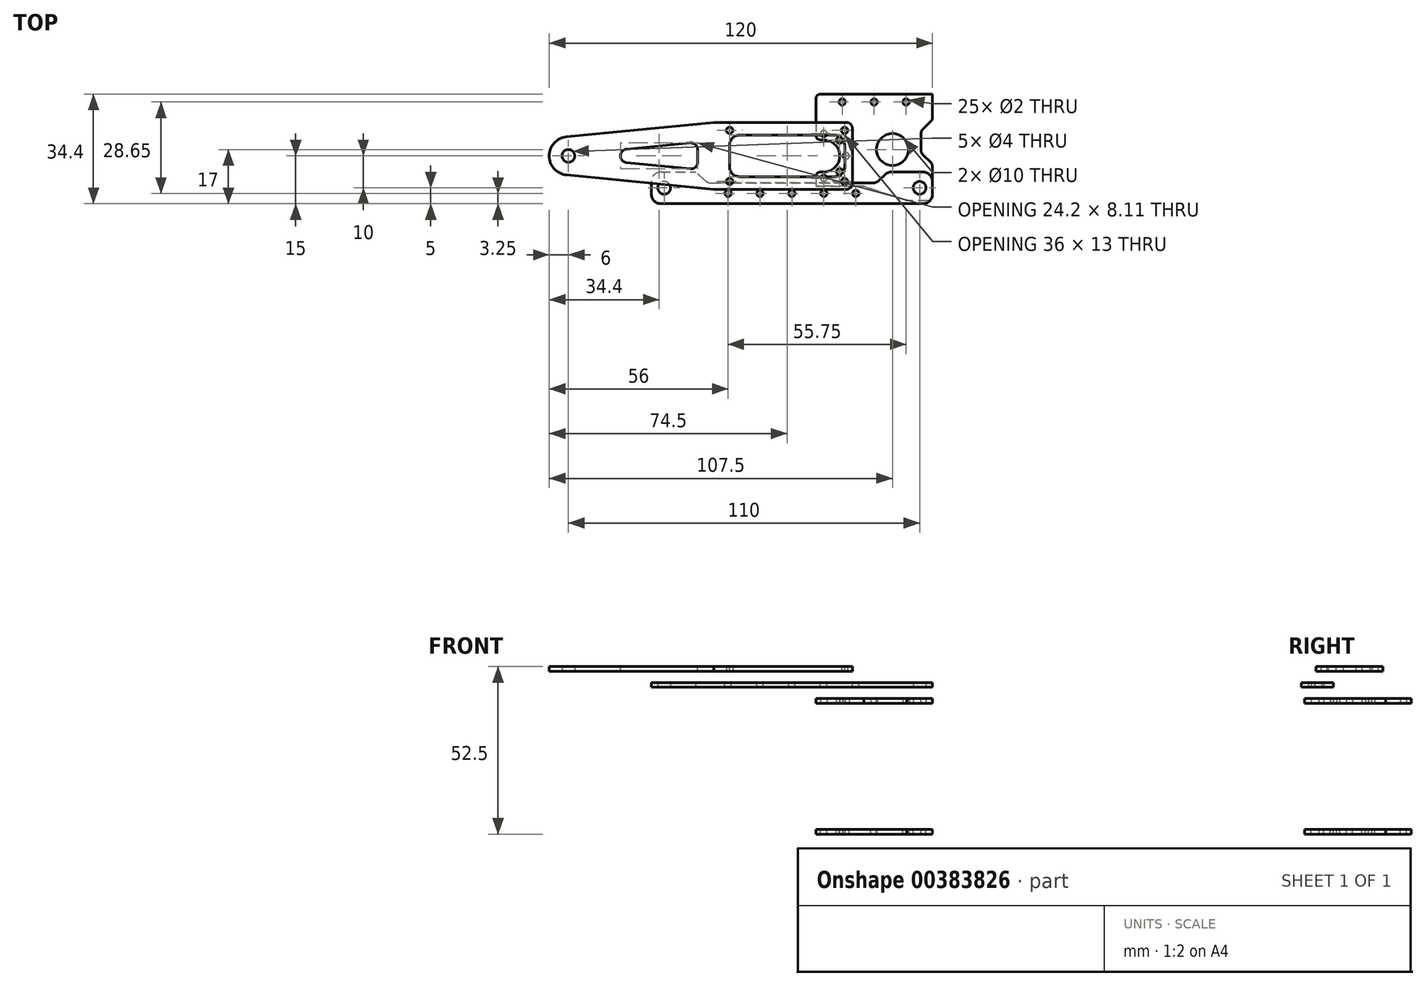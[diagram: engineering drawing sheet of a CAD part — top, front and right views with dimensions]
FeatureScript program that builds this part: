
annotation { "Feature Type Name" : "Feature", "Feature Type Description" : "" }
export const myFeature = defineFeature(function(context is Context, id is Id, definition is map)
    precondition{}
    {
        {
            var Q0;
            Q0=qCreatedBy(makeId("Top.planeOp"),FACE);
            var sketch = newSketch(context, id + "F0", { "sketchPlane" : qUnion([Q0])});
            skLineSegment(sketch, "E0.bottom", {"start": v(18.25, 16) * mm, "end": v(-18.25, 16) * mm});
            skLineSegment(sketch, "E0.top", {"start": v(18.25, -16) * mm, "end": v(-18.25, -16) * mm});
            skLineSegment(sketch, "E0.left", {"start": v(18.25, 16) * mm, "end": v(18.25, -16) * mm});
            skLineSegment(sketch, "E0.right", {"start": v(-18.25, 16) * mm, "end": v(-18.25, -16) * mm});
            skPoint(sketch, "E0.middle", {"position": v(0, 0) * mm});
            skCircle(sketch, "E1", {"center": v(14.25, -12) * mm, "radius": 2 * mm});
            skArc(sketch, "E2", {"start": v(-18.25, 2.33) * mm, "mid": v(-20.75, -2) * mm, "end": v(-18.25, -6.33) * mm, "construction": true});
            skCircle(sketch, "E3", {"center": v(-22.75, -2) * mm, "radius": 1 * mm, "construction": true});
            skCircle(sketch, "E4.1.0", {"center": v(-20.7, -6.95) * mm, "radius": 1 * mm, "construction": true});
            skCircle(sketch, "E4.2.0", {"center": v(-15.75, -9) * mm, "radius": 1 * mm});
            skCircle(sketch, "E4.3.0", {"center": v(-10.8, -6.95) * mm, "radius": 1 * mm});
            skCircle(sketch, "E4.4.0", {"center": v(-8.75, -2) * mm, "radius": 1 * mm});
            skCircle(sketch, "E4.5.0", {"center": v(-10.8, 2.95) * mm, "radius": 1 * mm});
            skCircle(sketch, "E4.6.0", {"center": v(-15.75, 5) * mm, "radius": 1 * mm});
            skCircle(sketch, "E4.7.0", {"center": v(-20.7, 2.95) * mm, "radius": 1 * mm, "construction": true});
            skLineSegment(sketch, "E5", {"start": v(-15.75, 3) * mm, "end": v(-18.25, 3) * mm});
            skLineSegment(sketch, "E6", {"start": v(-15.75, -7) * mm, "end": v(-18.25, -7) * mm});
            skArc(sketch, "E7.trimOffspring", {"start": v(-15.75, -7) * mm, "mid": v(-10.75, -2) * mm, "end": v(-15.75, 3) * mm});
            skCircle(sketch, "E8", {"center": v(-10, 14.9) * mm, "radius": 1 * mm});
            skCircle(sketch, "E9.1.0.0", {"center": v(0, 14.9) * mm, "radius": 1 * mm});
            skCircle(sketch, "E9.2.0.0", {"center": v(10, 14.9) * mm, "radius": 1 * mm});
            skLineSegment(sketch, "E9.direction1", {"start": v(-10, 14.9) * mm, "end": v(0, 14.9) * mm, "construction": true});
            skSolve(sketch);
        }
        {
            var Q0;
            {var subQ3=sQuery(id+"F0.wireOp",EDGE,"E0.bottom");Q0=makeQuery(id+"F0.imprint","IMPRINT",FACE,{"disambiguationData":[TD([[makeQuery(id+"F0.imprint","IMPRINT",EDGE,{"derivedFrom":subQ3}),1.0]])]});}
            extrude(context, id + "F1", {"entities" : qUnion([Q0]), "depth" : 1.5 * mm});
        }
        {
            var Q0;
            Q0=makeQuery(id+"F1.opExtrude","CAP_FACE",FACE,{"disambiguationData":[OSD([sQuery(id+"F0.wireOp",EDGE,"E0.bottom"),sQuery(id+"F0.wireOp",EDGE,"E0.top"),sQuery(id+"F0.wireOp",EDGE,"E0.left"),sQuery(id+"F0.wireOp",EDGE,"E0.right"),sQuery(id+"F0.wireOp",EDGE,"E1"),sQuery(id+"F0.wireOp",EDGE,"E4.2.0"),sQuery(id+"F0.wireOp",EDGE,"E4.3.0"),sQuery(id+"F0.wireOp",EDGE,"E4.4.0"),sQuery(id+"F0.wireOp",EDGE,"E4.5.0"),sQuery(id+"F0.wireOp",EDGE,"E4.6.0"),sQuery(id+"F0.wireOp",EDGE,"E5"),sQuery(id+"F0.wireOp",EDGE,"E6"),sQuery(id+"F0.wireOp",EDGE,"E7.trimOffspring")])],"isStart":true});
            var sketch = newSketch(context, id + "F2", { "sketchPlane" : qUnion([Q0])});
            skLineSegment(sketch, "E10.bottom", {"start": v(18.25, -16) * mm, "end": v(-18.25, -16) * mm});
            skLineSegment(sketch, "E10.top", {"start": v(18.25, -17.4) * mm, "end": v(-18.25, -17.4) * mm});
            skLineSegment(sketch, "E10.left", {"start": v(18.25, -16) * mm, "end": v(18.25, -17.4) * mm});
            skLineSegment(sketch, "E10.right", {"start": v(-18.25, -16) * mm, "end": v(-18.25, -17.4) * mm});
            skSolve(sketch);
        }
        {
            var Q0;
            Q0 = qSketchRegion(id + "F2", true);
            extrude(context, id + "F3", {"entities" : qUnion([Q0]), "operationType" : NewBodyOperationType.ADD, "depth" : (39.5 / 2) * mm, "hasSecondDirection" : true, "secondDirectionOppositeDirection" : true, "secondDirectionDepth" : 1.5 * mm});
        }
        {
            var Q0;
            Q0=makeQuery(id+"F3.opExtrude","CAP_FACE",FACE,{"disambiguationData":[OSD([sQuery(id+"F2.wireOp",EDGE,"E10.bottom"),sQuery(id+"F2.wireOp",EDGE,"E10.top"),sQuery(id+"F2.wireOp",EDGE,"E10.left"),sQuery(id+"F2.wireOp",EDGE,"E10.right")])],"isStart":false});
            cPlane(context, id + "F4", {"entities" : qUnion([Q0]), "cplaneType" : CPlaneType.OFFSET, "offset" : 0 * mm, "width" : 150 * mm, "height" : 150 * mm});
        }
        {
            var Q0;
            Q0=makeQuery(id+"F1.opExtrude","SWEPT_BODY",BODY,{"disambiguationData":[OSD([sQuery(id+"F0.wireOp",EDGE,"E0.bottom"),sQuery(id+"F0.wireOp",EDGE,"E0.top"),sQuery(id+"F0.wireOp",EDGE,"E0.left"),sQuery(id+"F0.wireOp",EDGE,"E0.right"),sQuery(id+"F0.wireOp",EDGE,"E1"),sQuery(id+"F0.wireOp",EDGE,"E4.2.0"),sQuery(id+"F0.wireOp",EDGE,"E4.3.0"),sQuery(id+"F0.wireOp",EDGE,"E4.4.0"),sQuery(id+"F0.wireOp",EDGE,"E4.5.0"),sQuery(id+"F0.wireOp",EDGE,"E4.6.0"),sQuery(id+"F0.wireOp",EDGE,"E5"),sQuery(id+"F0.wireOp",EDGE,"E6"),sQuery(id+"F0.wireOp",EDGE,"E7.trimOffspring")])]});
            var Q1;
            Q1=qCreatedBy(id+"F4.planeOp",FACE);
            mirror(context, id + "F5", {"operationType" : NewBodyOperationType.ADD, "entities" : qUnion([Q0]), "mirrorPlane" : qUnion([Q1])});
        }
        {
            var Q0;
            {var subQ0=makeQuery(id+"F3.opExtrude","SWEPT_FACE",FACE,{"disambiguationData":[OSD([sQuery(id+"F2.wireOp",EDGE,"E10.top")])]});Q0=makeQuery(id+"F5.boolean.opBoolean","MERGE",FACE,{"derivedFrom":[subQ0,makeQuery(id+"F5.opPattern","COPY",FACE,{"derivedFrom":subQ0,"instanceName":"1"})]});}
            var sketch = newSketch(context, id + "F6", { "sketchPlane" : qUnion([Q0])});
            skPoint(sketch, "E11.firstSnap0", {"position": v(18.25, -19.75) * mm});
            skLineSegment(sketch, "E11.bottom", {"start": v(18.25, 0) * mm, "end": v(8.25, 0) * mm});
            skLineSegment(sketch, "E11.top", {"start": v(18.25, -39.5) * mm, "end": v(8.25, -39.5) * mm});
            skLineSegment(sketch, "E11.left", {"start": v(18.25, 0) * mm, "end": v(18.25, -39.5) * mm});
            skLineSegment(sketch, "E11.right", {"start": v(8.25, 0) * mm, "end": v(8.25, -39.5) * mm});
            skSolve(sketch);
        }
        {
            var Q0;
            Q0 = qSketchRegion(id + "F6", true);
            extrude(context, id + "F7", {"entities" : qUnion([Q0]), "operationType" : NewBodyOperationType.REMOVE, "endBound" : BoundingType.UP_TO_NEXT, "oppositeDirection" : true, "depth" : 25 * mm});
        }
        {
            var Q0;
            Q0=makeQuery(id+"F3.boolean.opBoolean","MERGE",FACE,{"derivedFrom":[makeQuery(id+"F1.opExtrude","CAP_FACE",FACE,{"disambiguationData":[OSD([sQuery(id+"F0.wireOp",EDGE,"E0.bottom"),sQuery(id+"F0.wireOp",EDGE,"E0.top"),sQuery(id+"F0.wireOp",EDGE,"E0.left"),sQuery(id+"F0.wireOp",EDGE,"E0.right"),sQuery(id+"F0.wireOp",EDGE,"E1"),sQuery(id+"F0.wireOp",EDGE,"E4.2.0"),sQuery(id+"F0.wireOp",EDGE,"E4.3.0"),sQuery(id+"F0.wireOp",EDGE,"E4.4.0"),sQuery(id+"F0.wireOp",EDGE,"E4.5.0"),sQuery(id+"F0.wireOp",EDGE,"E4.6.0"),sQuery(id+"F0.wireOp",EDGE,"E5"),sQuery(id+"F0.wireOp",EDGE,"E6"),sQuery(id+"F0.wireOp",EDGE,"E7.trimOffspring")])],"isStart":false}),makeQuery(id+"F3.opExtrude","CAP_FACE",FACE,{"disambiguationData":[OSD([sQuery(id+"F2.wireOp",EDGE,"E10.bottom"),sQuery(id+"F2.wireOp",EDGE,"E10.top"),sQuery(id+"F2.wireOp",EDGE,"E10.left"),sQuery(id+"F2.wireOp",EDGE,"E10.right")])],"isStart":true})]});
            var sketch = newSketch(context, id + "F8", { "sketchPlane" : qUnion([Q0])});
            skCircle(sketch, "E12", {"center": v(-15.75, -2) * mm, "radius": 10 * mm});
            skSolve(sketch);
        }
        {
            var Q0;
            Q0=qCreatedBy(makeId("Top.planeOp"),FACE);
            cPlane(context, id + "F9", {"entities" : qUnion([Q0]), "cplaneType" : CPlaneType.OFFSET, "offset" : 5 * mm, "width" : 150 * mm, "height" : 150 * mm});
        }
        {
            var Q0;
            Q0=qCreatedBy(id+"F9.planeOp",FACE);
            var sketch = newSketch(context, id + "F10", { "sketchPlane" : qUnion([Q0])});
            skCircle(sketch, "E13.0", {"center": v(14.25, -12) * mm, "radius": 2 * mm});
            skLineSegment(sketch, "E14.bottom", {"start": v(-69.75, -7) * mm, "end": v(18.25, -7) * mm});
            skLineSegment(sketch, "E14.top", {"start": v(-69.75, -17) * mm, "end": v(18.25, -17) * mm});
            skLineSegment(sketch, "E14.left", {"start": v(-69.75, -7) * mm, "end": v(-69.75, -17) * mm});
            skLineSegment(sketch, "E14.right", {"start": v(18.25, -7) * mm, "end": v(18.25, -17) * mm});
            skLineSegment(sketch, "E15", {"start": v(-25.75, -7) * mm, "end": v(-25.75, -17) * mm, "construction": true});
            skCircle(sketch, "E16.MirrorC", {"center": v(-65.75, -12) * mm, "radius": 2 * mm});
            skLineSegment(sketch, "E17.bottom", {"start": v(-40.75, -7) * mm, "end": v(-10.75, -7) * mm});
            skLineSegment(sketch, "E17.top", {"start": v(-40.75, -9) * mm, "end": v(-10.75, -9) * mm});
            skLineSegment(sketch, "E17.left", {"start": v(-40.75, -7) * mm, "end": v(-40.75, -9) * mm});
            skLineSegment(sketch, "E17.right", {"start": v(-10.75, -7) * mm, "end": v(-10.75, -9) * mm});
            skPoint(sketch, "E17.middle", {"position": v(-25.75, -8) * mm});
            skSolve(sketch);
        }
        {
            var Q0;
            Q0=makeQuery(id+"F10.imprint","IMPRINT",FACE,{"disambiguationData":[TD([[makeQuery(id+"F10.imprint","IMPRINT",EDGE,{"derivedFrom":sQuery(id+"F10.wireOp",EDGE,"E13.0")}),-1.0]])]});
            var Q1;
            Q1=makeQuery(id+"F10.imprint","IMPRINT",FACE,{"disambiguationData":[TD([[makeQuery(id+"F10.imprint","IMPRINT",EDGE,{"derivedFrom":sQuery(id+"F10.wireOp",EDGE,"E17.top")}),1.0]])]});
            extrude(context, id + "F11", {"entities" : qUnion([Q0, Q1]), "depth" : 1.5 * mm});
        }
        {
            var Q0;
            Q0=qCreatedBy(makeId("Top.planeOp"),FACE);
            cPlane(context, id + "F12", {"entities" : qUnion([Q0]), "cplaneType" : CPlaneType.OFFSET, "offset" : 10 * mm, "width" : 150 * mm, "height" : 150 * mm});
        }
        {
            var Q0;
            Q0=qCreatedBy(id+"F12.planeOp",FACE);
            var sketch = newSketch(context, id + "F13", { "sketchPlane" : qUnion([Q0])});
            skCircle(sketch, "E18.0", {"center": v(-15.75, -2) * mm, "radius": 10 * mm, "construction": true});
            skLineSegment(sketch, "E19.bottom", {"start": v(-45.25, 6) * mm, "end": v(-9.25, 6) * mm, "construction": true});
            skLineSegment(sketch, "E19.top", {"start": v(-45.25, -10) * mm, "end": v(-9.25, -10) * mm, "construction": true});
            skLineSegment(sketch, "E19.left", {"start": v(-45.25, 6) * mm, "end": v(-45.25, -10) * mm, "construction": true});
            skLineSegment(sketch, "E19.right", {"start": v(-9.25, 6) * mm, "end": v(-9.25, -10) * mm, "construction": true});
            skPoint(sketch, "E19.middle", {"position": v(-27.25, -2) * mm});
            skCircle(sketch, "E20", {"center": v(-9.25, 6) * mm, "radius": 1 * mm});
            skCircle(sketch, "E21", {"center": v(-9.25, -10) * mm, "radius": 1 * mm});
            skCircle(sketch, "E22", {"center": v(-45.25, -10) * mm, "radius": 1 * mm});
            skCircle(sketch, "E23", {"center": v(-45.25, 6) * mm, "radius": 1 * mm});
            skLineSegment(sketch, "E24.bottom", {"start": v(-6.75, -12.5) * mm, "end": v(-101.75, -12.5) * mm});
            skLineSegment(sketch, "E24.top", {"start": v(-6.75, 8.5) * mm, "end": v(-101.75, 8.5) * mm});
            skLineSegment(sketch, "E24.left", {"start": v(-6.75, -12.5) * mm, "end": v(-6.75, 8.5) * mm});
            skLineSegment(sketch, "E24.right", {"start": v(-101.75, -12.5) * mm, "end": v(-101.75, 8.5) * mm});
            skPoint(sketch, "E25", {"position": v(-6.75, -2) * mm});
            skCircle(sketch, "E26", {"center": v(-95.75, -2) * mm, "radius": 2 * mm});
            skLineSegment(sketch, "E27", {"start": v(-95.75, -2) * mm, "end": v(-15.75, -2) * mm, "construction": true});
            skCircle(sketch, "E28.0", {"center": v(-65.75, -12) * mm, "radius": 2 * mm, "construction": true});
            skCircle(sketch, "E29.0", {"center": v(14.25, -12) * mm, "radius": 2 * mm, "construction": true});
            skLineSegment(sketch, "E30", {"start": v(-65.75, -12) * mm, "end": v(14.25, -12) * mm, "construction": true});
            skSolve(sketch);
        }
        {
            var Q0;
            Q0 = qSketchRegion(id + "F13", true);
            extrude(context, id + "F14", {"entities" : qUnion([Q0]), "operationType" : NewBodyOperationType.ADD, "depth" : 1.5 * mm});
        }
        {
            var Q0;
            Q0=makeQuery(id+"F14.opExtrude","CAP_FACE",FACE,{"disambiguationData":[OSD([sQuery(id+"F13.wireOp",EDGE,"E20"),sQuery(id+"F13.wireOp",EDGE,"E21"),sQuery(id+"F13.wireOp",EDGE,"E22"),sQuery(id+"F13.wireOp",EDGE,"E23"),sQuery(id+"F13.wireOp",EDGE,"E24.bottom"),sQuery(id+"F13.wireOp",EDGE,"E24.top"),sQuery(id+"F13.wireOp",EDGE,"E24.left"),sQuery(id+"F13.wireOp",EDGE,"E24.right"),sQuery(id+"F13.wireOp",EDGE,"E26")])],"isStart":false});
            var sketch = newSketch(context, id + "F15", { "sketchPlane" : qUnion([Q0])});
            skCircle(sketch, "E31", {"center": v(-95.75, -2) * mm, "radius": 6 * mm});
            skLineSegment(sketch, "E32", {"start": v(-50.25, 8.5) * mm, "end": v(-96.34, 3.97) * mm});
            skLineSegment(sketch, "E33", {"start": v(-6.75, -2) * mm, "end": v(-101.75, -2) * mm, "construction": true});
            skLineSegment(sketch, "E34.MirrorCS", {"start": v(-50.25, -12.5) * mm, "end": v(-96.34, -7.97) * mm});
            skLineSegment(sketch, "E35", {"start": v(-50.25, 8.5) * mm, "end": v(-101.75, 8.5) * mm});
            skLineSegment(sketch, "E36", {"start": v(-101.75, 8.5) * mm, "end": v(-101.75, -12.5) * mm});
            skLineSegment(sketch, "E37", {"start": v(-101.75, -12.5) * mm, "end": v(-50.25, -12.5) * mm});
            skCircle(sketch, "E38.0", {"center": v(-45.25, -10) * mm, "radius": 1 * mm, "construction": true});
            skLineSegment(sketch, "E39", {"start": v(-77.56, 0.09) * mm, "end": v(-57.56, 2.06) * mm});
            skLineSegment(sketch, "E40", {"start": v(-55.25, -0.03) * mm, "end": v(-55.25, -2) * mm});
            skLineSegment(sketch, "E41.MirrorCS", {"start": v(-55.25, -3.97) * mm, "end": v(-55.25, -2) * mm});
            skLineSegment(sketch, "E42.MirrorCS", {"start": v(-77.56, -4.09) * mm, "end": v(-57.56, -6.06) * mm});
            skPoint(sketch, "E43.visualSharp", {"position": v(-55.25, 2.28) * mm});
            skArc(sketch, "E43.filletArc", {"start": v(-55.25, -0.03) * mm, "mid": v(-55.94, 1.52) * mm, "end": v(-57.56, 2.06) * mm});
            skPoint(sketch, "E44.visualSharp", {"position": v(-55.25, -6.28) * mm});
            skArc(sketch, "E44.filletArc", {"start": v(-57.56, -6.06) * mm, "mid": v(-55.94, -5.52) * mm, "end": v(-55.25, -3.97) * mm});
            skPoint(sketch, "E45.visualSharp", {"position": v(-98.82, -2) * mm});
            skArc(sketch, "E45.filletArc", {"start": v(-77.56, 0.09) * mm, "mid": v(-79.45, -2) * mm, "end": v(-77.56, -4.09) * mm});
            skSolve(sketch);
        }
        {
            var Q0;
            {var subQ0=sQuery(id+"F15.wireOp",EDGE,"E32");Q0=makeQuery(id+"F15.imprint","IMPRINT",FACE,{"disambiguationData":[TD([[makeQuery(id+"F15.imprint","IMPRINT",EDGE,{"derivedFrom":subQ0}),-1.0]])]});}
            var Q1;
            {var subQ0=sQuery(id+"F15.wireOp",EDGE,"E34.MirrorCS");Q1=makeQuery(id+"F15.imprint","IMPRINT",FACE,{"disambiguationData":[TD([[makeQuery(id+"F15.imprint","IMPRINT",EDGE,{"derivedFrom":subQ0}),1.0]])]});}
            var Q2;
            Q2=makeQuery(id+"F15.imprint","IMPRINT",FACE,{"disambiguationData":[TD([[makeQuery(id+"F15.imprint","IMPRINT",EDGE,{"derivedFrom":sQuery(id+"F15.wireOp",EDGE,"E39")}),-1.0]])]});
            extrude(context, id + "F16", {"entities" : qUnion([Q0, Q1, Q2]), "operationType" : NewBodyOperationType.REMOVE, "endBound" : BoundingType.UP_TO_NEXT, "oppositeDirection" : true, "depth" : 25 * mm});
        }
        {
            var Q0;
            Q0=qCreatedBy(makeId("Top.planeOp"),FACE);
            cPlane(context, id + "F17", {"entities" : qUnion([Q0]), "cplaneType" : CPlaneType.OFFSET, "offset" : 50 * mm, "oppositeDirection" : true, "width" : 150 * mm, "height" : 150 * mm});
        }
        {
            var Q0;
            Q0=makeQuery(id+"F1.opExtrude","SWEPT_BODY",BODY,{"disambiguationData":[OSD([sQuery(id+"F0.wireOp",EDGE,"E0.bottom"),sQuery(id+"F0.wireOp",EDGE,"E0.top"),sQuery(id+"F0.wireOp",EDGE,"E0.left"),sQuery(id+"F0.wireOp",EDGE,"E0.right"),sQuery(id+"F0.wireOp",EDGE,"E1"),sQuery(id+"F0.wireOp",EDGE,"E4.2.0"),sQuery(id+"F0.wireOp",EDGE,"E4.3.0"),sQuery(id+"F0.wireOp",EDGE,"E4.4.0"),sQuery(id+"F0.wireOp",EDGE,"E4.5.0"),sQuery(id+"F0.wireOp",EDGE,"E4.6.0"),sQuery(id+"F0.wireOp",EDGE,"E5"),sQuery(id+"F0.wireOp",EDGE,"E6"),sQuery(id+"F0.wireOp",EDGE,"E7.trimOffspring")])]});
            var Q1;
            Q1=qCreatedBy(id+"F17.planeOp",FACE);
            mirror(context, id + "F18", {"entities" : qUnion([Q0]), "mirrorPlane" : qUnion([Q1])});
        }
        {
            var Q0;
            Q0=makeQuery(id+"F3.boolean.opBoolean","MERGE",FACE,{"derivedFrom":[makeQuery(id+"F1.opExtrude","CAP_FACE",FACE,{"disambiguationData":[OSD([sQuery(id+"F0.wireOp",EDGE,"E0.bottom"),sQuery(id+"F0.wireOp",EDGE,"E0.top"),sQuery(id+"F0.wireOp",EDGE,"E0.left"),sQuery(id+"F0.wireOp",EDGE,"E0.right"),sQuery(id+"F0.wireOp",EDGE,"E1"),sQuery(id+"F0.wireOp",EDGE,"E4.2.0"),sQuery(id+"F0.wireOp",EDGE,"E4.3.0"),sQuery(id+"F0.wireOp",EDGE,"E4.4.0"),sQuery(id+"F0.wireOp",EDGE,"E4.5.0"),sQuery(id+"F0.wireOp",EDGE,"E4.6.0"),sQuery(id+"F0.wireOp",EDGE,"E5"),sQuery(id+"F0.wireOp",EDGE,"E6"),sQuery(id+"F0.wireOp",EDGE,"E7.trimOffspring")])],"isStart":false}),makeQuery(id+"F3.opExtrude","CAP_FACE",FACE,{"disambiguationData":[OSD([sQuery(id+"F2.wireOp",EDGE,"E10.bottom"),sQuery(id+"F2.wireOp",EDGE,"E10.top"),sQuery(id+"F2.wireOp",EDGE,"E10.left"),sQuery(id+"F2.wireOp",EDGE,"E10.right")])],"isStart":true})]});
            var sketch = newSketch(context, id + "F19", { "sketchPlane" : qUnion([Q0])});
            skCircle(sketch, "E46.0", {"center": v(-15.75, -9) * mm, "radius": 1 * mm, "construction": true});
            skLineSegment(sketch, "E47", {"start": v(-18.25, -11.5) * mm, "end": v(-3.25, -11.5) * mm});
            skLineSegment(sketch, "E48", {"start": v(-3.25, -11.5) * mm, "end": v(10.25, -16) * mm});
            skCircle(sketch, "E49.0", {"center": v(14.25, -12) * mm, "radius": 2 * mm, "construction": true});
            skLineSegment(sketch, "E50", {"start": v(18.25, 9.4) * mm, "end": v(14.75, 5.9) * mm});
            skLineSegment(sketch, "E51", {"start": v(14.75, 5.9) * mm, "end": v(14.75, 2.4) * mm});
            skLineSegment(sketch, "E52", {"start": v(14.75, 2.4) * mm, "end": v(18.25, 2.4) * mm, "construction": true});
            skLineSegment(sketch, "E53.MirrorCS", {"start": v(14.75, -1.1) * mm, "end": v(14.75, 2.4) * mm});
            skLineSegment(sketch, "E54.MirrorCS", {"start": v(18.25, -4.6) * mm, "end": v(14.75, -1.1) * mm});
            skLineSegment(sketch, "E55", {"start": v(18.25, 9.4) * mm, "end": v(18.25, -4.6) * mm});
            skCircle(sketch, "E56", {"center": v(5.75, 0) * mm, "radius": 5 * mm});
            skSolve(sketch);
        }
        {
            var Q0;
            Q0 = qSketchRegion(id + "F19", true);
            var Q1;
            {var subQ0=sQuery(id+"F19.wireOp",EDGE,"E47");Q1=makeQuery(id+"F19.imprint","IMPRINT",FACE,{"disambiguationData":[TD([[makeQuery(id+"F19.imprint","IMPRINT",EDGE,{"derivedFrom":subQ0}),-1.0]])]});}
            var Q2;
            Q2=makeQuery(id+"F18.opPattern","COPY",FACE,{"derivedFrom":makeQuery(id+"F3.boolean.opBoolean","MERGE",FACE,{"derivedFrom":[makeQuery(id+"F1.opExtrude","CAP_FACE",FACE,{"disambiguationData":[OSD([sQuery(id+"F0.wireOp",EDGE,"E0.bottom"),sQuery(id+"F0.wireOp",EDGE,"E0.top"),sQuery(id+"F0.wireOp",EDGE,"E0.left"),sQuery(id+"F0.wireOp",EDGE,"E0.right"),sQuery(id+"F0.wireOp",EDGE,"E1"),sQuery(id+"F0.wireOp",EDGE,"E4.2.0"),sQuery(id+"F0.wireOp",EDGE,"E4.3.0"),sQuery(id+"F0.wireOp",EDGE,"E4.4.0"),sQuery(id+"F0.wireOp",EDGE,"E4.5.0"),sQuery(id+"F0.wireOp",EDGE,"E4.6.0"),sQuery(id+"F0.wireOp",EDGE,"E5"),sQuery(id+"F0.wireOp",EDGE,"E6"),sQuery(id+"F0.wireOp",EDGE,"E7.trimOffspring")])],"isStart":false}),makeQuery(id+"F3.opExtrude","CAP_FACE",FACE,{"disambiguationData":[OSD([sQuery(id+"F2.wireOp",EDGE,"E10.bottom"),sQuery(id+"F2.wireOp",EDGE,"E10.top"),sQuery(id+"F2.wireOp",EDGE,"E10.left"),sQuery(id+"F2.wireOp",EDGE,"E10.right")])],"isStart":true})]}),"instanceName":"1"});
            extrude(context, id + "F20", {"entities" : qUnion([Q0, Q1]), "operationType" : NewBodyOperationType.REMOVE, "endBound" : BoundingType.THROUGH_ALL, "oppositeDirection" : true, "endBoundEntityFace" : qUnion([Q2]), "depth" : 25 * mm});
        }
        {
            var Q0;
            Q0=makeQuery(id+"F11.opExtrude","CAP_FACE",FACE,{"disambiguationData":[OSD([sQuery(id+"F10.wireOp",EDGE,"E13.0"),sQuery(id+"F10.wireOp",EDGE,"E14.bottom"),sQuery(id+"F10.wireOp",EDGE,"E14.top"),sQuery(id+"F10.wireOp",EDGE,"E14.left"),sQuery(id+"F10.wireOp",EDGE,"E14.right"),sQuery(id+"F10.wireOp",EDGE,"E16.MirrorC")])],"isStart":false});
            var sketch = newSketch(context, id + "F21", { "sketchPlane" : qUnion([Q0])});
            skLineSegment(sketch, "E57", {"start": v(-55.75, -7) * mm, "end": v(-52.25, -10.5) * mm});
            skLineSegment(sketch, "E58", {"start": v(-52.25, -10.5) * mm, "end": v(-25.75, -10.5) * mm});
            skLineSegment(sketch, "E59", {"start": v(-25.75, -7) * mm, "end": v(-25.75, -17) * mm, "construction": true});
            skLineSegment(sketch, "E60", {"start": v(-69.75, -12) * mm, "end": v(18.25, -12) * mm, "construction": true});
            skCircle(sketch, "E61.0", {"center": v(-65.75, -12) * mm, "radius": 2 * mm, "construction": true});
            skLineSegment(sketch, "E62.MirrorCS", {"start": v(0.75, -10.5) * mm, "end": v(-25.75, -10.5) * mm});
            skLineSegment(sketch, "E63.MirrorCS", {"start": v(4.25, -7) * mm, "end": v(0.75, -10.5) * mm});
            skLineSegment(sketch, "E64", {"start": v(-55.75, -7) * mm, "end": v(4.25, -7) * mm});
            skSolve(sketch);
        }
        {
            var Q0;
            Q0 = qSketchRegion(id + "F21", true);
            extrude(context, id + "F22", {"entities" : qUnion([Q0]), "operationType" : NewBodyOperationType.REMOVE, "endBound" : BoundingType.UP_TO_NEXT, "oppositeDirection" : true, "depth" : 25 * mm});
        }
        {
            var Q0;
            Q0=makeQuery(id+"F11.opExtrude","SWEPT_EDGE",EDGE,{"disambiguationData":[OSD([sQuery(id+"F10.wireOp",EDGE,"E14.bottom"),sQuery(id+"F10.wireOp",EDGE,"E14.left")])]});
            var Q1;
            Q1=makeQuery(id+"F11.opExtrude","SWEPT_EDGE",EDGE,{"disambiguationData":[OSD([sQuery(id+"F10.wireOp",EDGE,"E14.top"),sQuery(id+"F10.wireOp",EDGE,"E14.left")])]});
            var Q2;
            Q2=makeQuery(id+"F11.opExtrude","SWEPT_EDGE",EDGE,{"disambiguationData":[OSD([sQuery(id+"F10.wireOp",EDGE,"E14.bottom"),sQuery(id+"F10.wireOp",EDGE,"E14.right")])]});
            var Q3;
            Q3=makeQuery(id+"F11.opExtrude","SWEPT_EDGE",EDGE,{"disambiguationData":[OSD([sQuery(id+"F10.wireOp",EDGE,"E14.top"),sQuery(id+"F10.wireOp",EDGE,"E14.right")])]});
            var Q4;
            Q4=makeQuery(id+"F22.boolean.opBoolean","COPY",EDGE,{"derivedFrom":makeQuery(id+"F22.opExtrude","SWEPT_EDGE",EDGE,{"disambiguationData":[OSD([sQuery(id+"F10.wireOp",EDGE,"E14.bottom"),sQuery(id+"F21.wireOp",EDGE,"E57"),sQuery(id+"F21.wireOp",EDGE,"E64")])]})});
            var Q5;
            Q5=makeQuery(id+"F22.boolean.opBoolean","COPY",EDGE,{"derivedFrom":makeQuery(id+"F22.opExtrude","SWEPT_EDGE",EDGE,{"disambiguationData":[OSD([sQuery(id+"F21.wireOp",EDGE,"E57"),sQuery(id+"F21.wireOp",EDGE,"E58")])]})});
            var Q6;
            Q6=makeQuery(id+"F22.boolean.opBoolean","COPY",EDGE,{"derivedFrom":makeQuery(id+"F22.opExtrude","SWEPT_EDGE",EDGE,{"disambiguationData":[OSD([sQuery(id+"F21.wireOp",EDGE,"E62.MirrorCS"),sQuery(id+"F21.wireOp",EDGE,"E63.MirrorCS")])]})});
            var Q7;
            Q7=makeQuery(id+"F22.boolean.opBoolean","COPY",EDGE,{"derivedFrom":makeQuery(id+"F22.opExtrude","SWEPT_EDGE",EDGE,{"disambiguationData":[OSD([sQuery(id+"F10.wireOp",EDGE,"E14.bottom"),sQuery(id+"F21.wireOp",EDGE,"E63.MirrorCS"),sQuery(id+"F21.wireOp",EDGE,"E64")])]})});
            fillet(context, id + "F23", {"entities" : qUnion([Q0, Q1, Q2, Q3, Q4, Q5, Q6, Q7]), "radius" : 3 * mm, "tangentPropagation" : true, "allowEdgeOverflow" : false});
        }
        {
            var Q0;
            Q0=makeQuery(id+"F14.opExtrude","CAP_FACE",FACE,{"disambiguationData":[OSD([sQuery(id+"F13.wireOp",EDGE,"E20"),sQuery(id+"F13.wireOp",EDGE,"E21"),sQuery(id+"F13.wireOp",EDGE,"E22"),sQuery(id+"F13.wireOp",EDGE,"E23"),sQuery(id+"F13.wireOp",EDGE,"E24.bottom"),sQuery(id+"F13.wireOp",EDGE,"E24.top"),sQuery(id+"F13.wireOp",EDGE,"E24.left"),sQuery(id+"F13.wireOp",EDGE,"E24.right"),sQuery(id+"F13.wireOp",EDGE,"E26")])],"isStart":false});
            var sketch = newSketch(context, id + "F24", { "sketchPlane" : qUnion([Q0])});
            skLineSegment(sketch, "E65.bottom", {"start": v(-42.25, 4.5) * mm, "end": v(-12.25, 4.5) * mm});
            skLineSegment(sketch, "E65.top", {"start": v(-42.25, -8.5) * mm, "end": v(-12.25, -8.5) * mm});
            skLineSegment(sketch, "E65.left", {"start": v(-45.25, 1.5) * mm, "end": v(-45.25, -5.5) * mm});
            skLineSegment(sketch, "E65.right", {"start": v(-9.25, 1.5) * mm, "end": v(-9.25, -5.5) * mm});
            skPoint(sketch, "E65.middle", {"position": v(-27.25, -2) * mm});
            skPoint(sketch, "E65.middle.positionSnap0", {"position": v(-6.75, -2) * mm});
            skPoint(sketch, "E65.centerSnap0", {"position": v(-6.75, -2) * mm});
            skLineSegment(sketch, "E66", {"start": v(-45.25, 6) * mm, "end": v(-9.25, 6) * mm, "construction": true});
            skPoint(sketch, "E67", {"position": v(-27.25, 6) * mm});
            skPoint(sketch, "E68.visualSharp", {"position": v(-45.25, 4.5) * mm});
            skArc(sketch, "E68.filletArc", {"start": v(-42.25, 4.5) * mm, "mid": v(-44.37, 3.62) * mm, "end": v(-45.25, 1.5) * mm});
            skPoint(sketch, "E69.visualSharp", {"position": v(-45.25, -8.5) * mm});
            skArc(sketch, "E69.filletArc", {"start": v(-45.25, -5.5) * mm, "mid": v(-44.37, -7.62) * mm, "end": v(-42.25, -8.5) * mm});
            skPoint(sketch, "E70.visualSharp", {"position": v(-9.25, 4.5) * mm});
            skArc(sketch, "E70.filletArc", {"start": v(-9.25, 1.5) * mm, "mid": v(-10.13, 3.62) * mm, "end": v(-12.25, 4.5) * mm});
            skPoint(sketch, "E71.visualSharp", {"position": v(-9.25, -8.5) * mm});
            skArc(sketch, "E71.filletArc", {"start": v(-12.25, -8.5) * mm, "mid": v(-10.13, -7.62) * mm, "end": v(-9.25, -5.5) * mm});
            skLineSegment(sketch, "E72", {"start": v(-95.75, -2) * mm, "end": v(-45.25, -2) * mm, "construction": true});
            skSolve(sketch);
        }
        {
            var Q0;
            Q0=makeQuery(id+"F24.imprint","IMPRINT",FACE,{"disambiguationData":[TD([[makeQuery(id+"F24.imprint","IMPRINT",EDGE,{"derivedFrom":sQuery(id+"F24.wireOp",EDGE,"E65.bottom")}),-1.0]])]});
            extrude(context, id + "F25", {"entities" : qUnion([Q0]), "operationType" : NewBodyOperationType.REMOVE, "endBound" : BoundingType.UP_TO_NEXT, "oppositeDirection" : true, "depth" : 25 * mm, "offsetDistance" : 25 * mm});
        }
        {
            var Q0;
            Q0=makeQuery(id+"F16.boolean.opBoolean","COPY",EDGE,{"derivedFrom":makeQuery(id+"F16.opExtrude","SWEPT_EDGE",EDGE,{"disambiguationData":[OSD([sQuery(id+"F13.wireOp",EDGE,"E24.top"),sQuery(id+"F15.wireOp",EDGE,"E32"),sQuery(id+"F15.wireOp",EDGE,"E35")])]})});
            var Q1;
            Q1=makeQuery(id+"F16.boolean.opBoolean","COPY",EDGE,{"derivedFrom":makeQuery(id+"F16.opExtrude","SWEPT_EDGE",EDGE,{"disambiguationData":[OSD([sQuery(id+"F13.wireOp",EDGE,"E24.bottom"),sQuery(id+"F15.wireOp",EDGE,"E34.MirrorCS"),sQuery(id+"F15.wireOp",EDGE,"E37")])]})});
            var Q2;
            Q2=makeQuery(id+"F14.opExtrude","SWEPT_EDGE",EDGE,{"disambiguationData":[OSD([sQuery(id+"F13.wireOp",EDGE,"E24.bottom"),sQuery(id+"F13.wireOp",EDGE,"E24.left")])]});
            var Q3;
            Q3=makeQuery(id+"F14.opExtrude","SWEPT_EDGE",EDGE,{"disambiguationData":[OSD([sQuery(id+"F13.wireOp",EDGE,"E24.top"),sQuery(id+"F13.wireOp",EDGE,"E24.left")])]});
            fillet(context, id + "F26", {"entities" : qUnion([Q0, Q1, Q2, Q3]), "radius" : 2 * mm, "tangentPropagation" : true, "allowEdgeOverflow" : false});
        }
        {
            var Q0;
            {var subQ0=sQuery(id+"F0.wireOp",EDGE,"E0.right");var subQ1=sQuery(id+"F19.wireOp",EDGE,"E47");Q0=makeQuery(id+"F20.boolean.opBoolean","COPY",EDGE,{"disambiguationData":[topologyDisambiguationEdgeConnected([makeQuery(id+"F5.opPattern","COPY",FACE,{"derivedFrom":makeQuery(id+"F1.opExtrude","SWEPT_FACE",FACE,{"disambiguationData":[OSD([subQ0]),TDD([makeQuery(id+"F0.imprint","IMPRINT",EDGE,{"disambiguationData":[TD([[makeQuery(id+"F0.imprint","INTERSECT",VERTEX,{"derivedFrom":[sQuery(id+"F0.wireOp",EDGE,"E0.top"),subQ0]}),1.0]])],"derivedFrom":subQ0})])]}),"instanceName":"1"})])],"derivedFrom":makeQuery(id+"F20.opExtrude","SWEPT_EDGE",EDGE,{"disambiguationData":[OSD([subQ0,subQ1])]})});}
            var Q1;
            {var subQ0=sQuery(id+"F0.wireOp",EDGE,"E9.2.0.0");var subQ1=sQuery(id+"F0.wireOp",EDGE,"E9.1.0.0");var subQ2=sQuery(id+"F0.wireOp",EDGE,"E8");var subQ3=sQuery(id+"F0.wireOp",EDGE,"E7.trimOffspring");var subQ4=sQuery(id+"F0.wireOp",EDGE,"E6");var subQ5=sQuery(id+"F0.wireOp",EDGE,"E5");var subQ6=sQuery(id+"F0.wireOp",EDGE,"E4.6.0");var subQ7=sQuery(id+"F0.wireOp",EDGE,"E4.5.0");var subQ8=sQuery(id+"F0.wireOp",EDGE,"E4.4.0");var subQ9=sQuery(id+"F0.wireOp",EDGE,"E4.3.0");var subQ10=sQuery(id+"F0.wireOp",EDGE,"E4.2.0");var subQ11=sQuery(id+"F0.wireOp",EDGE,"E1");var subQ12=sQuery(id+"F0.wireOp",EDGE,"E0.right");var subQ13=sQuery(id+"F0.wireOp",EDGE,"E0.left");var subQ14=sQuery(id+"F0.wireOp",EDGE,"E0.top");var subQ15=sQuery(id+"F0.wireOp",EDGE,"E0.bottom");var subQ16=sQuery(id+"F19.wireOp",EDGE,"E47");var subQ17=sQuery(id+"F19.wireOp",EDGE,"E48");Q1=makeQuery(id+"F20.boolean.opBoolean","COPY",EDGE,{"disambiguationData":[TD([makeQuery(id+"F5.opPattern","COPY",FACE,{"derivedFrom":makeQuery(id+"F1.opExtrude","CAP_FACE",FACE,{"disambiguationData":[OSD([subQ15,subQ14,subQ13,subQ12,subQ11,subQ10,subQ9,subQ8,subQ7,subQ6,subQ5,subQ4,subQ3,subQ2,subQ1,subQ0])],"isStart":true}),"instanceName":"1"})])],"derivedFrom":makeQuery(id+"F20.opExtrude","SWEPT_EDGE",EDGE,{"disambiguationData":[OSD([subQ16,subQ17])]})});}
            var Q2;
            {var subQ0=sQuery(id+"F0.wireOp",EDGE,"E0.top");var subQ1=sQuery(id+"F19.wireOp",EDGE,"E48");Q2=makeQuery(id+"F20.boolean.opBoolean","COPY",EDGE,{"disambiguationData":[topologyDisambiguationEdgeConnected([makeQuery(id+"F5.opPattern","COPY",FACE,{"derivedFrom":makeQuery(id+"F1.opExtrude","SWEPT_FACE",FACE,{"disambiguationData":[OSD([subQ0])]}),"instanceName":"1"})])],"derivedFrom":makeQuery(id+"F20.opExtrude","SWEPT_EDGE",EDGE,{"disambiguationData":[OSD([subQ0,subQ1])]})});}
            var Q3;
            Q3=makeQuery(id+"F5.opPattern","COPY",EDGE,{"derivedFrom":makeQuery(id+"F1.opExtrude","SWEPT_EDGE",EDGE,{"disambiguationData":[OSD([sQuery(id+"F0.wireOp",EDGE,"E0.top"),sQuery(id+"F0.wireOp",EDGE,"E0.left")])]}),"instanceName":"1"});
            var Q4;
            {var subQ0=sQuery(id+"F2.wireOp",EDGE,"E10.left");var subQ1=sQuery(id+"F0.wireOp",EDGE,"E9.2.0.0");var subQ2=sQuery(id+"F0.wireOp",EDGE,"E9.1.0.0");var subQ3=sQuery(id+"F0.wireOp",EDGE,"E8");var subQ4=sQuery(id+"F0.wireOp",EDGE,"E7.trimOffspring");var subQ5=sQuery(id+"F0.wireOp",EDGE,"E6");var subQ6=sQuery(id+"F0.wireOp",EDGE,"E5");var subQ7=sQuery(id+"F0.wireOp",EDGE,"E4.6.0");var subQ8=sQuery(id+"F0.wireOp",EDGE,"E4.5.0");var subQ9=sQuery(id+"F0.wireOp",EDGE,"E4.4.0");var subQ10=sQuery(id+"F0.wireOp",EDGE,"E4.3.0");var subQ11=sQuery(id+"F0.wireOp",EDGE,"E4.2.0");var subQ12=sQuery(id+"F0.wireOp",EDGE,"E1");var subQ13=sQuery(id+"F0.wireOp",EDGE,"E0.right");var subQ14=sQuery(id+"F0.wireOp",EDGE,"E0.left");var subQ15=sQuery(id+"F0.wireOp",EDGE,"E0.top");var subQ16=sQuery(id+"F0.wireOp",EDGE,"E0.bottom");var subQ17=makeQuery(id+"F3.opExtrude","SWEPT_FACE",FACE,{"disambiguationData":[OSD([subQ0])]});var subQ18=makeQuery(id+"F1.opExtrude","SWEPT_FACE",FACE,{"disambiguationData":[OSD([subQ14])]});var subQ19=sQuery(id+"F19.wireOp",EDGE,"E54.MirrorCS");var subQ20=makeQuery(id+"F20.opExtrude","SWEPT_FACE",FACE,{"disambiguationData":[OSD([subQ19])]});var subQ21=makeQuery(id+"F5.opPattern","COPY",FACE,{"derivedFrom":makeQuery(id+"F3.boolean.opBoolean","MERGE",FACE,{"derivedFrom":[subQ18,subQ17]}),"instanceName":"1"});Q4=makeQuery(id+"F20.boolean.opBoolean","COPY",EDGE,{"disambiguationData":[topologyDisambiguationEdgeConnected([subQ18,subQ17,subQ21,subQ20]),TD([makeQuery(id+"F5.opPattern","COPY",FACE,{"derivedFrom":makeQuery(id+"F1.opExtrude","CAP_FACE",FACE,{"disambiguationData":[OSD([subQ16,subQ15,subQ14,subQ13,subQ12,subQ11,subQ10,subQ9,subQ8,subQ7,subQ6,subQ5,subQ4,subQ3,subQ2,subQ1])],"isStart":true}),"instanceName":"1"})])],"derivedFrom":makeQuery(id+"F20.opExtrude","SWEPT_EDGE",EDGE,{"disambiguationData":[OSD([subQ14,subQ0,subQ19,sQuery(id+"F19.wireOp",EDGE,"E55")])]})});}
            var Q5;
            {var subQ0=sQuery(id+"F0.wireOp",EDGE,"E9.2.0.0");var subQ1=sQuery(id+"F0.wireOp",EDGE,"E9.1.0.0");var subQ2=sQuery(id+"F0.wireOp",EDGE,"E8");var subQ3=sQuery(id+"F0.wireOp",EDGE,"E7.trimOffspring");var subQ4=sQuery(id+"F0.wireOp",EDGE,"E6");var subQ5=sQuery(id+"F0.wireOp",EDGE,"E5");var subQ6=sQuery(id+"F0.wireOp",EDGE,"E4.6.0");var subQ7=sQuery(id+"F0.wireOp",EDGE,"E4.5.0");var subQ8=sQuery(id+"F0.wireOp",EDGE,"E4.4.0");var subQ9=sQuery(id+"F0.wireOp",EDGE,"E4.3.0");var subQ10=sQuery(id+"F0.wireOp",EDGE,"E4.2.0");var subQ11=sQuery(id+"F0.wireOp",EDGE,"E1");var subQ12=sQuery(id+"F0.wireOp",EDGE,"E0.right");var subQ13=sQuery(id+"F0.wireOp",EDGE,"E0.left");var subQ14=sQuery(id+"F0.wireOp",EDGE,"E0.top");var subQ15=sQuery(id+"F0.wireOp",EDGE,"E0.bottom");var subQ16=sQuery(id+"F19.wireOp",EDGE,"E53.MirrorCS");var subQ17=sQuery(id+"F19.wireOp",EDGE,"E54.MirrorCS");Q5=makeQuery(id+"F20.boolean.opBoolean","COPY",EDGE,{"disambiguationData":[TD([makeQuery(id+"F5.opPattern","COPY",FACE,{"derivedFrom":makeQuery(id+"F1.opExtrude","CAP_FACE",FACE,{"disambiguationData":[OSD([subQ15,subQ14,subQ13,subQ12,subQ11,subQ10,subQ9,subQ8,subQ7,subQ6,subQ5,subQ4,subQ3,subQ2,subQ1,subQ0])],"isStart":true}),"instanceName":"1"})])],"derivedFrom":makeQuery(id+"F20.opExtrude","SWEPT_EDGE",EDGE,{"disambiguationData":[OSD([subQ16,subQ17])]})});}
            var Q6;
            {var subQ0=sQuery(id+"F0.wireOp",EDGE,"E9.2.0.0");var subQ1=sQuery(id+"F0.wireOp",EDGE,"E9.1.0.0");var subQ2=sQuery(id+"F0.wireOp",EDGE,"E8");var subQ3=sQuery(id+"F0.wireOp",EDGE,"E7.trimOffspring");var subQ4=sQuery(id+"F0.wireOp",EDGE,"E6");var subQ5=sQuery(id+"F0.wireOp",EDGE,"E5");var subQ6=sQuery(id+"F0.wireOp",EDGE,"E4.6.0");var subQ7=sQuery(id+"F0.wireOp",EDGE,"E4.5.0");var subQ8=sQuery(id+"F0.wireOp",EDGE,"E4.4.0");var subQ9=sQuery(id+"F0.wireOp",EDGE,"E4.3.0");var subQ10=sQuery(id+"F0.wireOp",EDGE,"E4.2.0");var subQ11=sQuery(id+"F0.wireOp",EDGE,"E1");var subQ12=sQuery(id+"F0.wireOp",EDGE,"E0.right");var subQ13=sQuery(id+"F0.wireOp",EDGE,"E0.left");var subQ14=sQuery(id+"F0.wireOp",EDGE,"E0.top");var subQ15=sQuery(id+"F0.wireOp",EDGE,"E0.bottom");var subQ16=sQuery(id+"F19.wireOp",EDGE,"E50");var subQ17=sQuery(id+"F19.wireOp",EDGE,"E51");Q6=makeQuery(id+"F20.boolean.opBoolean","COPY",EDGE,{"disambiguationData":[TD([makeQuery(id+"F5.opPattern","COPY",FACE,{"derivedFrom":makeQuery(id+"F1.opExtrude","CAP_FACE",FACE,{"disambiguationData":[OSD([subQ15,subQ14,subQ13,subQ12,subQ11,subQ10,subQ9,subQ8,subQ7,subQ6,subQ5,subQ4,subQ3,subQ2,subQ1,subQ0])],"isStart":true}),"instanceName":"1"})])],"derivedFrom":makeQuery(id+"F20.opExtrude","SWEPT_EDGE",EDGE,{"disambiguationData":[OSD([subQ16,subQ17])]})});}
            var Q7;
            {var subQ0=sQuery(id+"F2.wireOp",EDGE,"E10.left");var subQ1=sQuery(id+"F0.wireOp",EDGE,"E9.2.0.0");var subQ2=sQuery(id+"F0.wireOp",EDGE,"E9.1.0.0");var subQ3=sQuery(id+"F0.wireOp",EDGE,"E8");var subQ4=sQuery(id+"F0.wireOp",EDGE,"E7.trimOffspring");var subQ5=sQuery(id+"F0.wireOp",EDGE,"E6");var subQ6=sQuery(id+"F0.wireOp",EDGE,"E5");var subQ7=sQuery(id+"F0.wireOp",EDGE,"E4.6.0");var subQ8=sQuery(id+"F0.wireOp",EDGE,"E4.5.0");var subQ9=sQuery(id+"F0.wireOp",EDGE,"E4.4.0");var subQ10=sQuery(id+"F0.wireOp",EDGE,"E4.3.0");var subQ11=sQuery(id+"F0.wireOp",EDGE,"E4.2.0");var subQ12=sQuery(id+"F0.wireOp",EDGE,"E1");var subQ13=sQuery(id+"F0.wireOp",EDGE,"E0.right");var subQ14=sQuery(id+"F0.wireOp",EDGE,"E0.left");var subQ15=sQuery(id+"F0.wireOp",EDGE,"E0.top");var subQ16=sQuery(id+"F0.wireOp",EDGE,"E0.bottom");var subQ17=makeQuery(id+"F3.opExtrude","SWEPT_FACE",FACE,{"disambiguationData":[OSD([subQ0])]});var subQ18=makeQuery(id+"F1.opExtrude","SWEPT_FACE",FACE,{"disambiguationData":[OSD([subQ14])]});var subQ19=makeQuery(id+"F5.opPattern","COPY",FACE,{"derivedFrom":makeQuery(id+"F3.boolean.opBoolean","MERGE",FACE,{"derivedFrom":[subQ18,subQ17]}),"instanceName":"1"});var subQ20=sQuery(id+"F19.wireOp",EDGE,"E50");var subQ21=makeQuery(id+"F20.opExtrude","SWEPT_FACE",FACE,{"disambiguationData":[OSD([subQ20])]});Q7=makeQuery(id+"F20.boolean.opBoolean","COPY",EDGE,{"disambiguationData":[topologyDisambiguationEdgeConnected([subQ18,subQ17,subQ19,subQ21]),TD([makeQuery(id+"F5.opPattern","COPY",FACE,{"derivedFrom":makeQuery(id+"F1.opExtrude","CAP_FACE",FACE,{"disambiguationData":[OSD([subQ16,subQ15,subQ14,subQ13,subQ12,subQ11,subQ10,subQ9,subQ8,subQ7,subQ6,subQ5,subQ4,subQ3,subQ2,subQ1])],"isStart":true}),"instanceName":"1"})])],"derivedFrom":makeQuery(id+"F20.opExtrude","SWEPT_EDGE",EDGE,{"disambiguationData":[OSD([subQ14,subQ0,subQ20,sQuery(id+"F19.wireOp",EDGE,"E55")])]})});}
            var Q8;
            {var subQ0=sQuery(id+"F0.wireOp",EDGE,"E0.top");var subQ1=sQuery(id+"F19.wireOp",EDGE,"E48");Q8=makeQuery(id+"F20.boolean.opBoolean","COPY",EDGE,{"disambiguationData":[topologyDisambiguationEdgeConnected([makeQuery(id+"F1.opExtrude","SWEPT_FACE",FACE,{"disambiguationData":[OSD([subQ0])]})])],"derivedFrom":makeQuery(id+"F20.opExtrude","SWEPT_EDGE",EDGE,{"disambiguationData":[OSD([subQ0,subQ1])]})});}
            var Q9;
            Q9=makeQuery(id+"F1.opExtrude","SWEPT_EDGE",EDGE,{"disambiguationData":[OSD([sQuery(id+"F0.wireOp",EDGE,"E0.top"),sQuery(id+"F0.wireOp",EDGE,"E0.left")])]});
            var Q10;
            {var subQ0=sQuery(id+"F2.wireOp",EDGE,"E10.left");var subQ14=sQuery(id+"F0.wireOp",EDGE,"E0.left");var subQ17=makeQuery(id+"F1.opExtrude","SWEPT_FACE",FACE,{"disambiguationData":[OSD([subQ14])]});var subQ18=sQuery(id+"F19.wireOp",EDGE,"E54.MirrorCS");var subQ19=makeQuery(id+"F20.opExtrude","SWEPT_FACE",FACE,{"disambiguationData":[OSD([subQ18])]});var subQ20=makeQuery(id+"F3.opExtrude","SWEPT_FACE",FACE,{"disambiguationData":[OSD([subQ0])]});var subQ21=makeQuery(id+"F5.opPattern","COPY",FACE,{"derivedFrom":makeQuery(id+"F3.boolean.opBoolean","MERGE",FACE,{"derivedFrom":[subQ17,subQ20]}),"instanceName":"1"});Q10=makeQuery(id+"F20.boolean.opBoolean","COPY",EDGE,{"disambiguationData":[topologyDisambiguationEdgeConnected([subQ17,subQ20,subQ21,subQ19]),TD([makeQuery(id+"F3.opExtrude","CAP_FACE",FACE,{"disambiguationData":[OSD([sQuery(id+"F2.wireOp",EDGE,"E10.bottom"),sQuery(id+"F2.wireOp",EDGE,"E10.top"),subQ0,sQuery(id+"F2.wireOp",EDGE,"E10.right")])],"isStart":true})])],"derivedFrom":makeQuery(id+"F20.opExtrude","SWEPT_EDGE",EDGE,{"disambiguationData":[OSD([subQ14,subQ0,subQ18,sQuery(id+"F19.wireOp",EDGE,"E55")])]})});}
            var Q11;
            {var subQ0=sQuery(id+"F19.wireOp",EDGE,"E53.MirrorCS");var subQ17=sQuery(id+"F19.wireOp",EDGE,"E54.MirrorCS");Q11=makeQuery(id+"F20.boolean.opBoolean","COPY",EDGE,{"disambiguationData":[TD([makeQuery(id+"F3.opExtrude","CAP_FACE",FACE,{"disambiguationData":[OSD([sQuery(id+"F2.wireOp",EDGE,"E10.bottom"),sQuery(id+"F2.wireOp",EDGE,"E10.top"),sQuery(id+"F2.wireOp",EDGE,"E10.left"),sQuery(id+"F2.wireOp",EDGE,"E10.right")])],"isStart":true})])],"derivedFrom":makeQuery(id+"F20.opExtrude","SWEPT_EDGE",EDGE,{"disambiguationData":[OSD([subQ0,subQ17])]})});}
            var Q12;
            {var subQ16=sQuery(id+"F19.wireOp",EDGE,"E50");var subQ17=sQuery(id+"F19.wireOp",EDGE,"E51");Q12=makeQuery(id+"F20.boolean.opBoolean","COPY",EDGE,{"disambiguationData":[TD([makeQuery(id+"F3.opExtrude","CAP_FACE",FACE,{"disambiguationData":[OSD([sQuery(id+"F2.wireOp",EDGE,"E10.bottom"),sQuery(id+"F2.wireOp",EDGE,"E10.top"),sQuery(id+"F2.wireOp",EDGE,"E10.left"),sQuery(id+"F2.wireOp",EDGE,"E10.right")])],"isStart":true})])],"derivedFrom":makeQuery(id+"F20.opExtrude","SWEPT_EDGE",EDGE,{"disambiguationData":[OSD([subQ16,subQ17])]})});}
            var Q13;
            {var subQ0=sQuery(id+"F2.wireOp",EDGE,"E10.left");var subQ14=sQuery(id+"F0.wireOp",EDGE,"E0.left");var subQ17=makeQuery(id+"F1.opExtrude","SWEPT_FACE",FACE,{"disambiguationData":[OSD([subQ14])]});var subQ18=makeQuery(id+"F3.opExtrude","SWEPT_FACE",FACE,{"disambiguationData":[OSD([subQ0])]});var subQ19=makeQuery(id+"F5.opPattern","COPY",FACE,{"derivedFrom":makeQuery(id+"F3.boolean.opBoolean","MERGE",FACE,{"derivedFrom":[subQ17,subQ18]}),"instanceName":"1"});var subQ20=sQuery(id+"F19.wireOp",EDGE,"E50");var subQ21=makeQuery(id+"F20.opExtrude","SWEPT_FACE",FACE,{"disambiguationData":[OSD([subQ20])]});Q13=makeQuery(id+"F20.boolean.opBoolean","COPY",EDGE,{"disambiguationData":[topologyDisambiguationEdgeConnected([subQ17,subQ18,subQ19,subQ21]),TD([makeQuery(id+"F3.opExtrude","CAP_FACE",FACE,{"disambiguationData":[OSD([sQuery(id+"F2.wireOp",EDGE,"E10.bottom"),sQuery(id+"F2.wireOp",EDGE,"E10.top"),subQ0,sQuery(id+"F2.wireOp",EDGE,"E10.right")])],"isStart":true})])],"derivedFrom":makeQuery(id+"F20.opExtrude","SWEPT_EDGE",EDGE,{"disambiguationData":[OSD([subQ14,subQ0,subQ20,sQuery(id+"F19.wireOp",EDGE,"E55")])]})});}
            var Q14;
            {var subQ0=sQuery(id+"F2.wireOp",EDGE,"E10.right");var subQ1=sQuery(id+"F2.wireOp",EDGE,"E10.top");var subQ21=makeQuery(id+"F3.opExtrude","SWEPT_EDGE",EDGE,{"disambiguationData":[OSD([subQ1,subQ0])]});Q14=makeQuery(id+"F7.boolean.opBoolean","SPLIT",EDGE,{"disambiguationData":[TD([makeQuery(id+"F7.opExtrude","SWEPT_FACE",FACE,{"disambiguationData":[OSD([sQuery(id+"F6.wireOp",EDGE,"E11.bottom")])]})])],"derivedFrom":makeQuery(id+"F5.boolean.opBoolean","MERGE",EDGE,{"derivedFrom":[subQ21,makeQuery(id+"F5.opPattern","COPY",EDGE,{"derivedFrom":subQ21,"instanceName":"1"})]})});}
            var Q15;
            Q15=makeQuery(id+"F1.opExtrude","SWEPT_EDGE",EDGE,{"disambiguationData":[OSD([sQuery(id+"F0.wireOp",EDGE,"E0.right"),sQuery(id+"F0.wireOp",EDGE,"E5")])]});
            var Q16;
            Q16=makeQuery(id+"F1.opExtrude","SWEPT_EDGE",EDGE,{"disambiguationData":[OSD([sQuery(id+"F0.wireOp",EDGE,"E0.right"),sQuery(id+"F0.wireOp",EDGE,"E6")])]});
            var Q17;
            {var subQ0=sQuery(id+"F0.wireOp",EDGE,"E0.right");var subQ1=sQuery(id+"F19.wireOp",EDGE,"E47");Q17=makeQuery(id+"F20.boolean.opBoolean","COPY",EDGE,{"disambiguationData":[topologyDisambiguationEdgeConnected([makeQuery(id+"F1.opExtrude","SWEPT_FACE",FACE,{"disambiguationData":[OSD([subQ0]),TDD([makeQuery(id+"F0.imprint","IMPRINT",EDGE,{"disambiguationData":[TD([[makeQuery(id+"F0.imprint","INTERSECT",VERTEX,{"derivedFrom":[sQuery(id+"F0.wireOp",EDGE,"E0.top"),subQ0]}),1.0]])],"derivedFrom":subQ0})])]})])],"derivedFrom":makeQuery(id+"F20.opExtrude","SWEPT_EDGE",EDGE,{"disambiguationData":[OSD([subQ0,subQ1])]})});}
            var Q18;
            Q18=makeQuery(id+"F5.opPattern","COPY",EDGE,{"derivedFrom":makeQuery(id+"F1.opExtrude","SWEPT_EDGE",EDGE,{"disambiguationData":[OSD([sQuery(id+"F0.wireOp",EDGE,"E0.right"),sQuery(id+"F0.wireOp",EDGE,"E6")])]}),"instanceName":"1"});
            var Q19;
            Q19=makeQuery(id+"F5.opPattern","COPY",EDGE,{"derivedFrom":makeQuery(id+"F1.opExtrude","SWEPT_EDGE",EDGE,{"disambiguationData":[OSD([sQuery(id+"F0.wireOp",EDGE,"E0.right"),sQuery(id+"F0.wireOp",EDGE,"E5")])]}),"instanceName":"1"});
            var Q20;
            {var subQ0=sQuery(id+"F2.wireOp",EDGE,"E10.right");var subQ18=sQuery(id+"F2.wireOp",EDGE,"E10.top");var subQ21=makeQuery(id+"F3.opExtrude","SWEPT_EDGE",EDGE,{"disambiguationData":[OSD([subQ18,subQ0])]});Q20=makeQuery(id+"F7.boolean.opBoolean","SPLIT",EDGE,{"disambiguationData":[TD([makeQuery(id+"F7.opExtrude","SWEPT_FACE",FACE,{"disambiguationData":[OSD([sQuery(id+"F6.wireOp",EDGE,"E11.top")])]})])],"derivedFrom":makeQuery(id+"F5.boolean.opBoolean","MERGE",EDGE,{"derivedFrom":[subQ21,makeQuery(id+"F5.opPattern","COPY",EDGE,{"derivedFrom":subQ21,"instanceName":"1"})]})});}
            fillet(context, id + "F27", {"entities" : qUnion([Q0, Q1, Q2, Q3, Q4, Q5, Q6, Q7, Q8, Q9, Q10, Q11, Q12, Q13, Q14, Q15, Q16, Q17, Q18, Q19, Q20]), "radius" : 1.5 * mm, "tangentPropagation" : true, "allowEdgeOverflow" : false});
        }
        {
            var Q0;
            Q0=makeQuery(id+"F18.opPattern","COPY",BODY,{"derivedFrom":makeQuery(id+"F1.opExtrude","SWEPT_BODY",BODY,{"disambiguationData":[OSD([sQuery(id+"F0.wireOp",EDGE,"E0.bottom"),sQuery(id+"F0.wireOp",EDGE,"E0.top"),sQuery(id+"F0.wireOp",EDGE,"E0.left"),sQuery(id+"F0.wireOp",EDGE,"E0.right"),sQuery(id+"F0.wireOp",EDGE,"E1"),sQuery(id+"F0.wireOp",EDGE,"E4.2.0"),sQuery(id+"F0.wireOp",EDGE,"E4.3.0"),sQuery(id+"F0.wireOp",EDGE,"E4.4.0"),sQuery(id+"F0.wireOp",EDGE,"E4.5.0"),sQuery(id+"F0.wireOp",EDGE,"E4.6.0"),sQuery(id+"F0.wireOp",EDGE,"E5"),sQuery(id+"F0.wireOp",EDGE,"E6"),sQuery(id+"F0.wireOp",EDGE,"E7.trimOffspring")])]}),"instanceName":"1"});
            deleteBodies(context, id + "F28", {"entities" : qUnion([Q0])});
        }
        {
            var Q0;
            {var subQ0=makeQuery(id+"F3.opExtrude","SWEPT_FACE",FACE,{"disambiguationData":[OSD([sQuery(id+"F2.wireOp",EDGE,"E10.bottom")])]});Q0=makeQuery(id+"F5.boolean.opBoolean","MERGE",FACE,{"derivedFrom":[subQ0,makeQuery(id+"F5.opPattern","COPY",FACE,{"derivedFrom":subQ0,"instanceName":"1"})]});}
            var sketch = newSketch(context, id + "F29", { "sketchPlane" : qUnion([Q0])});
            skLineSegment(sketch, "E73.bottom", {"start": v(18.25, -39.5) * mm, "end": v(-18.25, -39.5) * mm});
            skLineSegment(sketch, "E73.top", {"start": v(18.25, 0) * mm, "end": v(-18.25, 0) * mm});
            skLineSegment(sketch, "E73.left", {"start": v(18.25, -39.5) * mm, "end": v(18.25, 0) * mm});
            skLineSegment(sketch, "E73.right", {"start": v(-18.25, -39.5) * mm, "end": v(-18.25, 0) * mm});
            skPoint(sketch, "E74.0", {"position": v(-18.25, 1.5) * mm});
            skSolve(sketch);
        }
        {
            var Q0;
            Q0 = qSketchRegion(id + "F29", true);
            extrude(context, id + "F30", {"entities" : qUnion([Q0]), "operationType" : NewBodyOperationType.ADD, "depth" : (5 - 1.4) * mm});
        }
        {
            var Q0;
            Q0=makeQuery(id+"F30.opExtrude","CAP_FACE",FACE,{"disambiguationData":[OSD([sQuery(id+"F29.wireOp",EDGE,"E73.bottom"),sQuery(id+"F29.wireOp",EDGE,"E73.top"),sQuery(id+"F29.wireOp",EDGE,"E73.left"),sQuery(id+"F29.wireOp",EDGE,"E73.right")])],"isStart":false});
            extrude(context, id + "F31", {"entities" : qUnion([Q0]), "operationType" : NewBodyOperationType.REMOVE, "oppositeDirection" : true, "depth" : 5 * mm});
        }
        {
            var Q0;
            Q0=makeQuery(id+"F11.opExtrude","CAP_FACE",FACE,{"disambiguationData":[OSD([sQuery(id+"F10.wireOp",EDGE,"E13.0"),sQuery(id+"F10.wireOp",EDGE,"E14.bottom"),sQuery(id+"F10.wireOp",EDGE,"E14.top"),sQuery(id+"F10.wireOp",EDGE,"E14.left"),sQuery(id+"F10.wireOp",EDGE,"E14.right"),sQuery(id+"F10.wireOp",EDGE,"E16.MirrorC")])],"isStart":false});
            var sketch = newSketch(context, id + "F32", { "sketchPlane" : qUnion([Q0])});
            skLineSegment(sketch, "E75", {"start": v(-65.75, -12) * mm, "end": v(14.25, -12) * mm, "construction": true});
            skLineSegment(sketch, "E76", {"start": v(-25.75, -17) * mm, "end": v(-25.75, -10.5) * mm, "construction": true});
            skCircle(sketch, "E77", {"center": v(-25.75, -13.75) * mm, "radius": 1 * mm});
            skCircle(sketch, "E78", {"center": v(-35.75, -13.75) * mm, "radius": 1 * mm});
            skCircle(sketch, "E79", {"center": v(-45.75, -13.75) * mm, "radius": 1 * mm});
            skCircle(sketch, "E80.MirrorC", {"center": v(-15.75, -13.75) * mm, "radius": 1 * mm});
            skCircle(sketch, "E81.MirrorC", {"center": v(-5.75, -13.75) * mm, "radius": 1 * mm});
            skSolve(sketch);
        }
        {
            var Q0;
            Q0 = qSketchRegion(id + "F32", true);
            extrude(context, id + "F33", {"entities" : qUnion([Q0]), "operationType" : NewBodyOperationType.REMOVE, "endBound" : BoundingType.UP_TO_NEXT, "oppositeDirection" : true, "depth" : 25 * mm, "offsetDistance" : 25 * mm});
        }
    });
